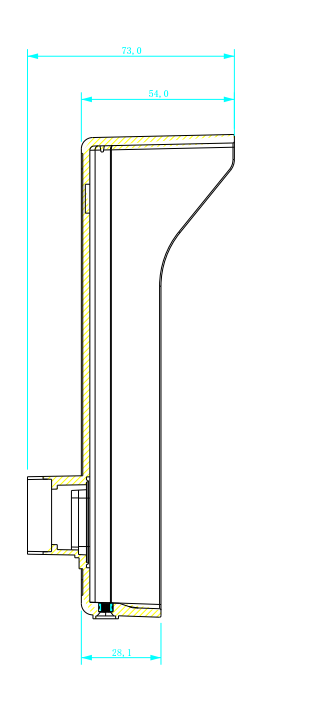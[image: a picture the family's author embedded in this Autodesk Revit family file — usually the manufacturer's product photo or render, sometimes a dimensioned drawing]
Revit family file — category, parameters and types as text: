
# Revit family: AZ-07LLF
name_source: partatom
category: Устройства связи
units: mm (PartAtom-declared; Revit-internal decimal feet)

## family parameters
Всегда вертикально = Нет
На основе рабочей плоскости = Да
Общий = Да
При загрузке вырезать с полостями = Нет
Размер круглого соединителя = Использовать диаметр
Сохранять ориентацию аннотаций = Нет
Тип детали = Нормальный
Точка расчета площади = Нет

## types (1)
- AZ-07LLF
    ADSK_URL документации изделия = https://drive.google.com
    ADSK_URL страницы изделия = https://bas-ip.com
    ADSK_Версия Revit = Revit 2020
    ADSK_Единица измерения = шт
    ADSK_Завод-изготовитель = BAS-IP
    ADSK_Классификация нагрузок = Внутренний монитор индивидуальный
    ADSK_Количество фаз = 1
    ADSK_Коэффициент мощности = 0.9
    ADSK_Марка = AZ-07LLF
    ADSK_Наименование = Внутренний монитор индивидуальный AZ-07LLF
    ADSK_Наименование краткое = AZ-07LLF
    ADSK_Напряжение = 12 В
    ADSK_Номинальная мощность = 3 Вт
    ADSK_Полная мощность = 3 В·А
    ADSK_Размер_Длина = 127 мм
    ADSK_Размер_Толщина = 27 мм
    ADSK_Размер_Ширина = 195 мм
    BIM library = https://bimlib.ru
    URL = https://www.bas-ip.ru
    Варианты монтажа = горизонтальный и вертикальный
    Встроенная камера = нет
    Выберите тип скринсейвера в режиме ожидания = просмотр одной IP-камеры в реальном времени
    Группа модели = Внутренний монитор индивидуальный
    Дополнительные разъемы = слот для карты SD (SDHC)
    Изготовитель = BAS-IP
    Изображение типоразмера = <Нет>
    Интерфейс = многоязычный графический и веб-интерфейс
    Количество IP-камер = до 8 камер
    Количество многоквартирных панелей = до 9 панелей
    Количество отдельных панелей = до 9 панелей
    Корпус = пластик
    Не беспокоить = да, настраивается по времени
    Обновление ПО = из веб-интерфейса; С сервера обновлений BAS-IP
    Описание = 7 дюймовый IP видеодомофон с настенным горизонтальным и вертикальным монтажом, возможностью управления лифтом, выводом сообщений от управляющей компании, PoE, подключением 8 камер, памятью для фото/видео и автоответчиком. ОС — Linux.
    Отметка по умолчанию = 0 мм
    Питание = PoE и +12 В постоянного тока (блок питания не входит в комплект)
    Поддержка получения сообщений = да
    Подключение дополнительных мониторов = до 8 мониторов
    Потребляемая мощность = 6 Вт, в режиме ожидания 2,5 Вт
    Размеры = 195х127х27 мм
    Разрешение экрана = 800 х 480
    Сетевое подключение = провод Ethernet UTP
    Тип домофона = видеодомофон, без встроенной камеры
    Тип установки = настенное крепление
    Тихий режим = да, настраивается по времени
    Функция памяти = запись фото во внутреннюю память (64 фото)
    Цветовое решение = черный/серый
    Экран = 7-дюймовый TFT LCD (емкостный сенсорный экран)
